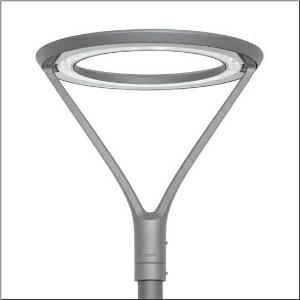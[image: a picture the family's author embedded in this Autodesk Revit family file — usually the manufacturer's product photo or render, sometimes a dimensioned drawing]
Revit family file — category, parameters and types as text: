
# Revit family: dl_r__20___pl1_2s_5xa512836s008_bfda
name_source: partatom
category: Lighting Fixtures
units: mm (PartAtom-declared; Revit-internal decimal feet)

## family parameters
Cut with Voids When Loaded = No
Host = Face
Light Source = No
Part Type = Normal
Room Calculation Point = No
Round Connector Dimension = Use Diameter
Shared = No

## types (1)
- --- (1 x LED, 3050 lm, 28.6 W, 2700K)
    Apparent Load = 29 VA
    CIE Flux Codes = 33 78 99 100 100
    Color Rendering = 70
    Color Temperature = 2700K
    Default Elevation = 1800 mm
    Description = DL® 20, mast luminaire, primary light control with reflector, highly specular, primary optical cover: cover, of toughened safety glass of clear glass with excellent transmission level, light distribution: PL1.2s, light emission: direct distribution, primary light characteristic: symmetric, installation type: post-top, LED, High Power LED, rated luminous flux: 3.050lm, luminous efficacy: 107lm/W, light colour: 727, colour temperature: 2700K, control gear: Plus, control: flexible luminous flux parameterisation, time-dependent luminous flux control, constant luminous flux control, digital communication interface, power reduction, overheat protection, electronic power reduction, mains connection: 220..240V, 50/60Hz, connection cable pre-assembled, cable length: 5m, start of lifetime: 29W, end of service life: 29W, reduction: 15W, luminaire housing, upper part, of cast aluminium, powder-coated, Siteco® metallic grey (DB 702S), diameter: 690mm, height: 690mm, spigot size: 76mm (post-top), mounting height: 4..6m, luminaire housing, of cast aluminium, powder-coated, Siteco® metallic grey (DB 702S), equipment: standard, protection rating (complete): IP66, insulation class (complete): insulation class II (safety insulation), certification: CE, ENEC, VDE, impact resistance: IK08, permissible operating ambient temperature: -25..+35°C, standard-compliant lighting for roads and squares, packaging unit: 1 piece

Light Distribution: PL1.2s
    Height = 690 mm
    Lamp = 1 x LED
    Lamp Light Flux = 3050 lm
    Lamp Power = 28.6 W
    Lamp count = 1
    Length = 690 mm
    Luminous efficacy = 107 lm/W
    Manufacturer = Siteco
    ModVariant = No
    Model = 5XA512836S008
    Number of Poles = 1
    OnlyDefault = Yes
    Power Factor = 1
    Product Name = DL® 20 | PL1.2s
    Product group = mast luminaire | pylon top
    ProductGroupID = 6100
    Protection Class = Protection class II
    Protection Degree = IP 66
    RLX_Detail_Level = 1
    RLX_Emergency_Light_Flux = 0 lm
    RLX_Emergency_Type = 0
    RLX_Emergency_Type_DB = No
    RlxData = <blob elided: 204493 chars, md5=91952d28>
    Socket = socket
    Standby Power = 0 W
    System Light Flux = 3050 lm
    System Power = 29 W
    Type Comments = factory setting: luminous flux: 100 % | dim-lin: 254 | 386 mA
    Type Image = l_1006001.jpg
    URL = http://relux.com
    VarID = @adj_076828
    Voltage = 0 V
    Weight = 0.00 kg
    Width = 0 mm  [stored 0 ft]

note: [stored X ft] marks values corroborated as IEEE doubles in the binary element streams (Revit-internal decimal feet)

## geometry (parser evidence)
native form markers: Blend x4, Sweep x9
no freeform markers — native parametric forms only
